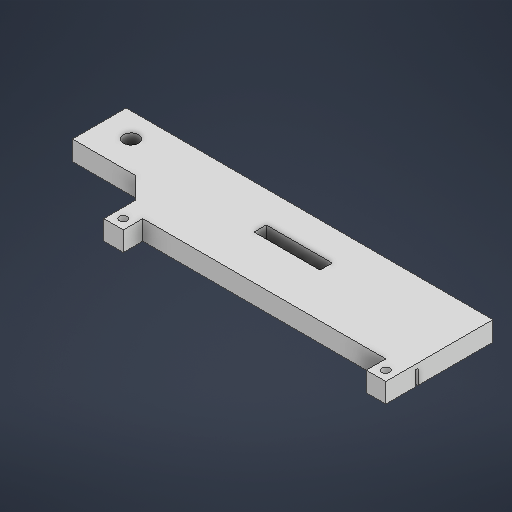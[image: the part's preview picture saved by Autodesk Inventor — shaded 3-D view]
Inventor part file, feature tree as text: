
AUTODESK INVENTOR PART (.ipt)
format: ipt  version: 2025 (Build 290162000, 162)  size: 294,912 bytes
history: native  units: mm
features: extrude x6, sketch x6, chamfer x2, projected_geometry x1
ambient origin geometry x8: Origin, YZ Plane, XZ Plane, XY Plane, X Axis, Y Axis, Z Axis, Center Point
bodies: Solid1 (feature_tree)
feature tree (15):
  extrude  "Extrusion1"  Depth=150.0mm
  extrude  "Extrusion2"  Depth=10.0mm
  extrude  "Extrusion3"  Depth=1.2mm
  extrude  "Extrusion4"  Depth=4.0mm
  extrude  "Extrusion5"  Depth=2.0mm
  extrude  "Extrusion6"  Depth=8.0mm
  chamfer  "Chamfer1"  Distance=8.0mm
  chamfer  "Chamfer2"  Distance=8.0mm
  sketch  "Sketch1"  dims[d3=20.0mm d4=150.0mm]
  sketch  "Sketch2"  dims[d7=10.0mm d8=6.2mm]
  projected_geometry  "Projected Loop1"
  sketch  "Sketch3"  dims[d9=6.0mm d10=0.0mm d11=1.2mm]
  sketch  "Sketch4"  dims[d12=2.0mm d13=0.0mm d14=4.0mm]
  sketch  "Sketch5"  dims[d15=2.0mm d16=0.0mm d17=2.0mm]
  sketch  "Sketch6"  dims[d18=45.0deg d19=8.0mm d20=8.0mm d21=8.0mm d22=8.0mm d23=3.2mm d24=3.2mm d25=10.0mm d26=0.0mm d27=11.5mm d28=7.0mm d29=23.0mm d30=29.5mm d31=6.0mm d32=6.0mm d33=3.2mm d34=3.2mm d35=6.0mm d36=0.0mm d37=6.0mm d38=2.5mm d39=20.0mm d40=5.0mm d41=18.75mm d42=0.0mm d43=7.0mm d44=2.0mm d45=45.0deg d46=1.0mm d47=2.0mm d48=45.0deg]
